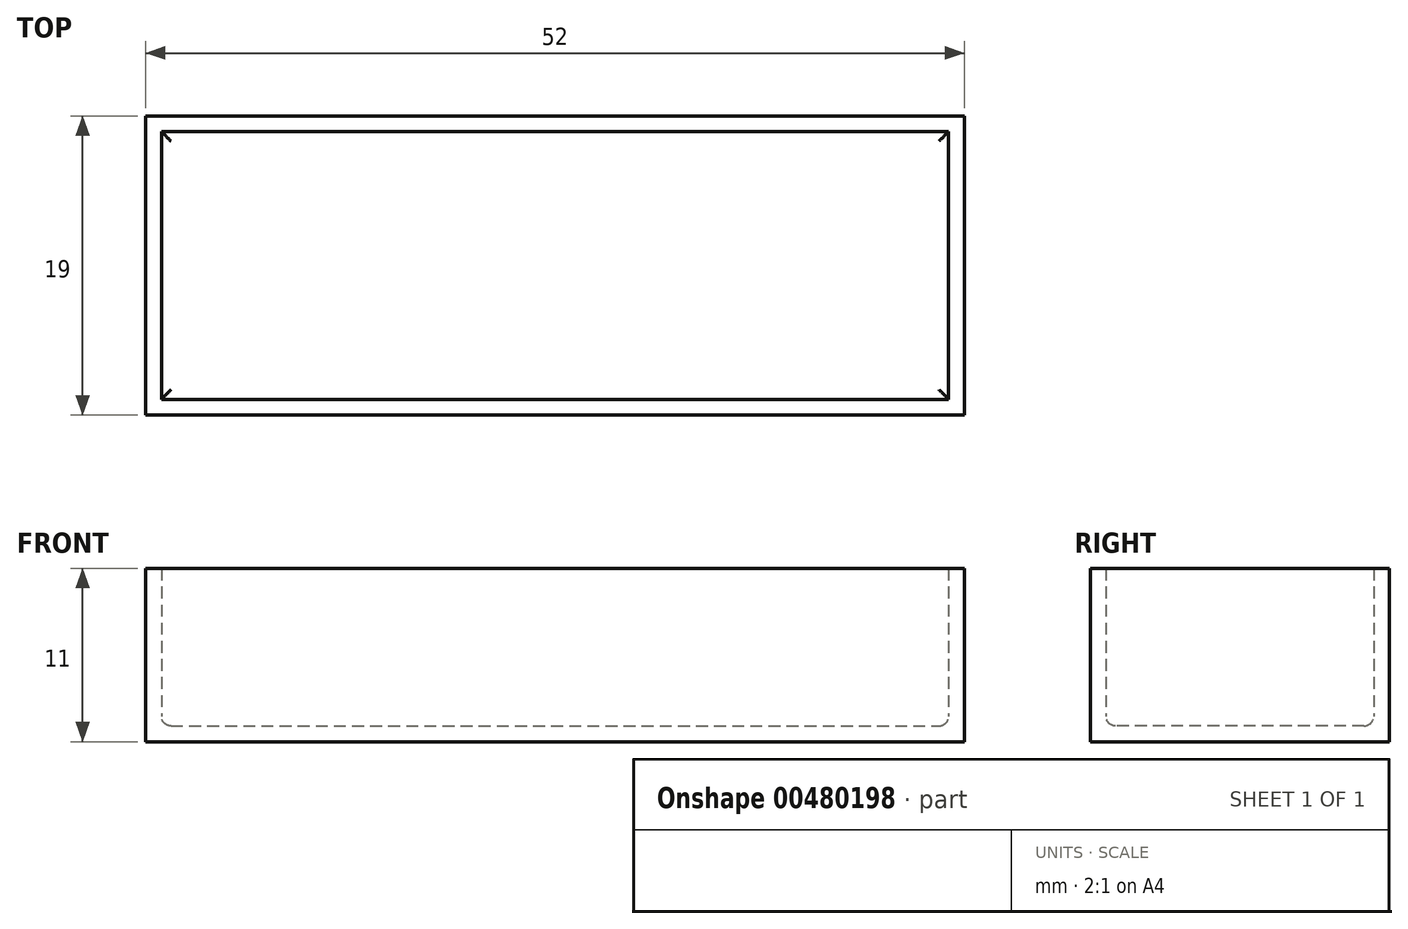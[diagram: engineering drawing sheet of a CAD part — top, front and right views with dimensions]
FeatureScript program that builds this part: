
annotation { "Feature Type Name" : "Feature", "Feature Type Description" : "" }
export const myFeature = defineFeature(function(context is Context, id is Id, definition is map)
    precondition{}
    {
        {
            var Q0;
            Q0=qCreatedBy(makeId("Top.planeOp"),FACE);
            var sketch = newSketch(context, id + "F0", { "sketchPlane" : qUnion([Q0])});
            skLineSegment(sketch, "E0.bottom", {"start": v(-18.1, 1.48) * mm, "end": v(31.9, 1.48) * mm});
            skLineSegment(sketch, "E0.top", {"start": v(-18.1, -15.52) * mm, "end": v(31.9, -15.52) * mm});
            skLineSegment(sketch, "E0.left", {"start": v(-18.1, 1.48) * mm, "end": v(-18.1, -15.52) * mm});
            skLineSegment(sketch, "E0.right", {"start": v(31.9, 1.48) * mm, "end": v(31.9, -15.52) * mm});
            skLineSegment(sketch, "E1.0", {"start": v(-19.1, 2.48) * mm, "end": v(32.9, 2.48) * mm});
            skLineSegment(sketch, "E1.1", {"start": v(-19.1, 2.48) * mm, "end": v(-19.1, -16.52) * mm});
            skLineSegment(sketch, "E1.2", {"start": v(-19.1, -16.52) * mm, "end": v(32.9, -16.52) * mm});
            skLineSegment(sketch, "E1.3", {"start": v(32.9, 2.48) * mm, "end": v(32.9, -16.52) * mm});
            skSolve(sketch);
        }
        {
            var Q0;
            Q0=makeQuery(id+"F0.imprint","IMPRINT",FACE,{"disambiguationData":[TD([[makeQuery(id+"F0.imprint","IMPRINT",EDGE,{"derivedFrom":sQuery(id+"F0.wireOp",EDGE,"E0.bottom")}),-1.0]])]});
            extrude(context, id + "F1", {"entities" : qUnion([Q0]), "depth" : 1 * mm});
        }
        {
            var Q0;
            Q0=makeQuery(id+"F0.imprint","IMPRINT",FACE,{"disambiguationData":[TD([[makeQuery(id+"F0.imprint","IMPRINT",EDGE,{"derivedFrom":sQuery(id+"F0.wireOp",EDGE,"E0.bottom")}),1.0]])]});
            extrude(context, id + "F2", {"entities" : qUnion([Q0]), "operationType" : NewBodyOperationType.ADD, "depth" : 11 * mm});
        }
        {
            var Q0;
            Q0=makeQuery(id+"F1.opExtrude","CAP_FACE",FACE,{"disambiguationData":[OSD([sQuery(id+"F0.wireOp",EDGE,"E0.bottom"),sQuery(id+"F0.wireOp",EDGE,"E0.top"),sQuery(id+"F0.wireOp",EDGE,"E0.left"),sQuery(id+"F0.wireOp",EDGE,"E0.right")])],"isStart":false});
            fillet(context, id + "F3", {"entities" : qUnion([Q0]), "radius" : 0.61 * mm, "tangentPropagation" : true, "allowEdgeOverflow" : false});
        }
    });
